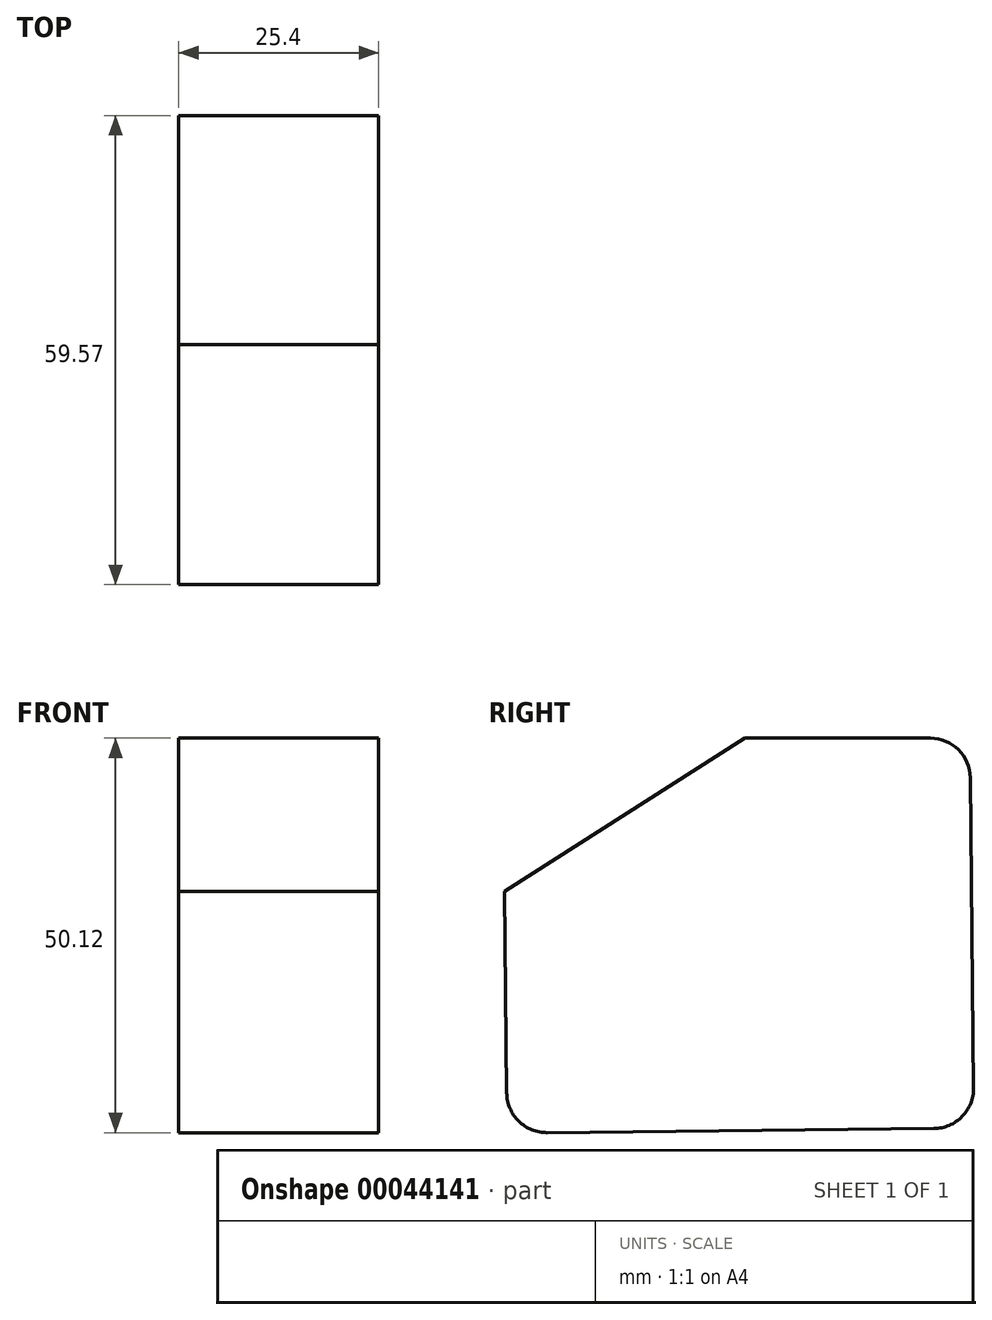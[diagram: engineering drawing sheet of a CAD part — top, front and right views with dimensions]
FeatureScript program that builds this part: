
annotation { "Feature Type Name" : "Feature", "Feature Type Description" : "" }
export const myFeature = defineFeature(function(context is Context, id is Id, definition is map)
    precondition{}
    {
        {
            var Q0;
            Q0=qCreatedBy(makeId("Right.planeOp"),FACE);
            cPlane(context, id + "F0", {"entities" : qUnion([Q0]), "cplaneType" : CPlaneType.OFFSET, "offset" : 152.4 * mm, "width" : 152.4 * mm, "height" : 152.4 * mm});
        }
        {
            var Q0;
            Q0=qCreatedBy(id+"F0.planeOp",FACE);
            var sketch = newSketch(context, id + "F1", { "sketchPlane" : qUnion([Q0])});
            skLineSegment(sketch, "E0", {"start": v(-59.1, 30.68) * mm, "end": v(-28.57, 50.17) * mm});
            skLineSegment(sketch, "E1", {"start": v(-28.57, 50.17) * mm, "end": v(0, 50.17) * mm});
            skLineSegment(sketch, "E2", {"start": v(-58.77, 0) * mm, "end": v(-59.1, 30.68) * mm});
            skLineSegment(sketch, "E3", {"start": v(-58.77, 0) * mm, "end": v(0.52, 0.63) * mm});
            skLineSegment(sketch, "E4", {"start": v(0.52, 0.63) * mm, "end": v(0, 50.17) * mm});
            skSolve(sketch);
        }
        {
            var Q0;
            Q0=makeQuery(id+"F1.imprint","IMPRINT",FACE,{"disambiguationData":[TD([[makeQuery(id+"F1.imprint","IMPRINT",EDGE,{"derivedFrom":sQuery(id+"F1.wireOp",EDGE,"E0")}),-1.0]])]});
            extrude(context, id + "F2", {"entities" : qUnion([Q0]), "depth" : 25.4 * mm});
        }
        {
            var Q0;
            Q0=makeQuery(id+"F2.opExtrude","SWEPT_EDGE",EDGE,{"disambiguationData":[OSD([sQuery(id+"F1.wireOp",EDGE,"E2"),sQuery(id+"F1.wireOp",EDGE,"E3")])]});
            fillet(context, id + "F3", {"entities" : qUnion([Q0]), "radius" : 5.08 * mm, "tangentPropagation" : true, "allowEdgeOverflow" : false});
        }
        {
            var Q0;
            Q0=makeQuery(id+"F2.opExtrude","SWEPT_EDGE",EDGE,{"disambiguationData":[OSD([sQuery(id+"F1.wireOp",EDGE,"E3"),sQuery(id+"F1.wireOp",EDGE,"E4")])]});
            var Q1;
            Q1=makeQuery(id+"F2.opExtrude","SWEPT_EDGE",EDGE,{"disambiguationData":[OSD([sQuery(id+"F1.wireOp",EDGE,"E1"),sQuery(id+"F1.wireOp",EDGE,"E4")])]});
            fillet(context, id + "F4", {"entities" : qUnion([Q0, Q1]), "radius" : 5.08 * mm, "tangentPropagation" : true, "allowEdgeOverflow" : false});
        }
    });
